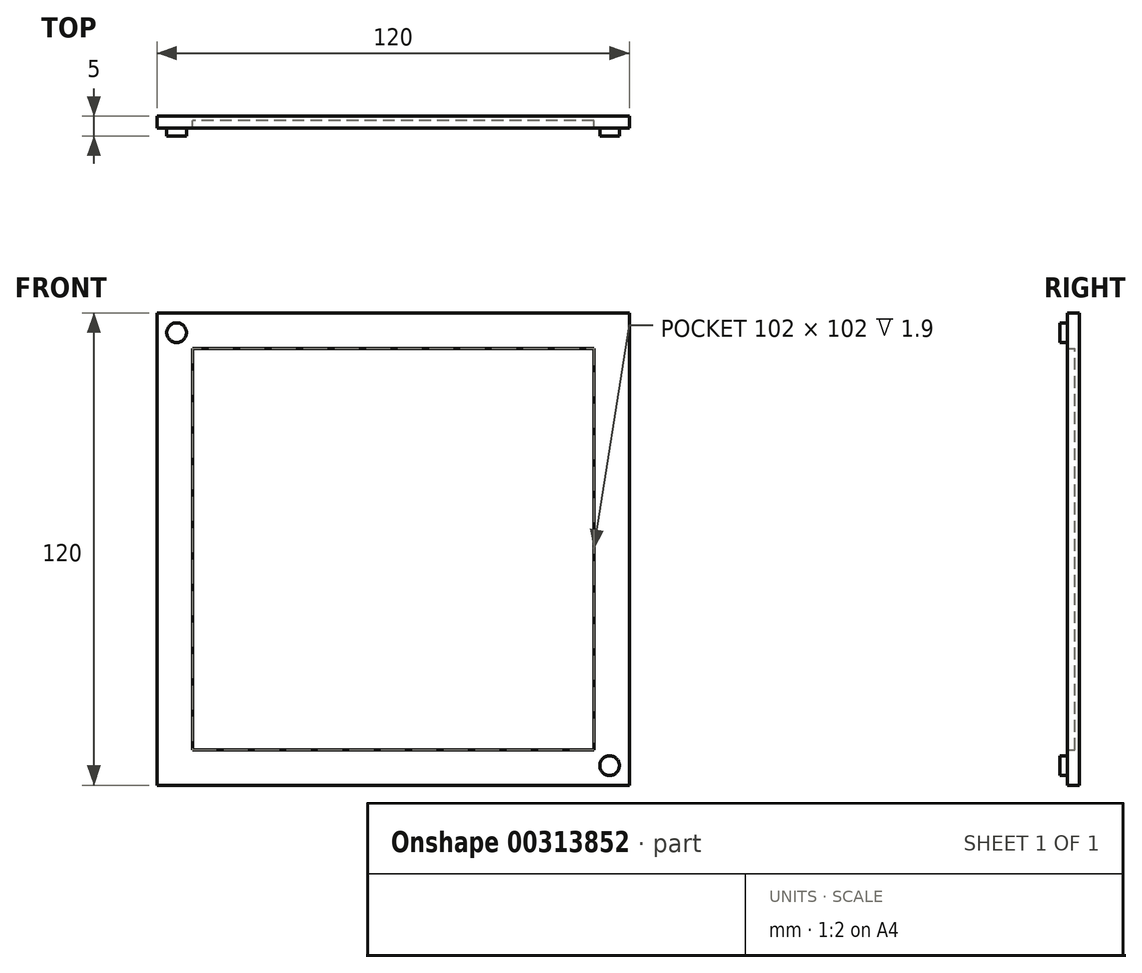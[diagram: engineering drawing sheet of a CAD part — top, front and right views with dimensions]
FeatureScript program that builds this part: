
annotation { "Feature Type Name" : "Feature", "Feature Type Description" : "" }
export const myFeature = defineFeature(function(context is Context, id is Id, definition is map)
    precondition{}
    {
        {
            var Q0;
            Q0=qCreatedBy(makeId("Front.planeOp"),FACE);
            var sketch = newSketch(context, id + "F0", { "sketchPlane" : qUnion([Q0])});
            skLineSegment(sketch, "E0.bottom", {"start": v(51, -51) * mm, "end": v(-51, -51) * mm});
            skLineSegment(sketch, "E0.top", {"start": v(51, 51) * mm, "end": v(-51, 51) * mm});
            skLineSegment(sketch, "E0.left", {"start": v(51, -51) * mm, "end": v(51, 51) * mm});
            skLineSegment(sketch, "E0.right", {"start": v(-51, -51) * mm, "end": v(-51, 51) * mm});
            skPoint(sketch, "E0.middle", {"position": v(0, 0) * mm});
            skLineSegment(sketch, "E1.bottom", {"start": v(60, -60) * mm, "end": v(-60, -60) * mm});
            skLineSegment(sketch, "E1.top", {"start": v(60, 60) * mm, "end": v(-60, 60) * mm});
            skLineSegment(sketch, "E1.left", {"start": v(60, -60) * mm, "end": v(60, 60) * mm});
            skLineSegment(sketch, "E1.right", {"start": v(-60, -60) * mm, "end": v(-60, 60) * mm});
            skSolve(sketch);
        }
        {
            var Q0;
            Q0=makeQuery(id+"F0.imprint","IMPRINT",FACE,{"disambiguationData":[TD([[makeQuery(id+"F0.imprint","IMPRINT",EDGE,{"derivedFrom":sQuery(id+"F0.wireOp",EDGE,"E0.bottom")}),1.0]])]});
            extrude(context, id + "F1", {"entities" : qUnion([Q0]), "depth" : 3 * mm});
        }
        {
            var Q0;
            Q0=makeQuery(id+"F0.imprint","IMPRINT",FACE,{"disambiguationData":[TD([[makeQuery(id+"F0.imprint","IMPRINT",EDGE,{"derivedFrom":sQuery(id+"F0.wireOp",EDGE,"E0.bottom")}),-1.0]])]});
            extrude(context, id + "F2", {"entities" : qUnion([Q0]), "operationType" : NewBodyOperationType.ADD, "depth" : 1.1 * mm});
        }
        {
            var Q0;
            Q0=makeQuery(id+"F1.opExtrude","CAP_FACE",FACE,{"disambiguationData":[OSD([sQuery(id+"F0.wireOp",EDGE,"E0.bottom"),sQuery(id+"F0.wireOp",EDGE,"E0.top"),sQuery(id+"F0.wireOp",EDGE,"E0.left"),sQuery(id+"F0.wireOp",EDGE,"E0.right"),sQuery(id+"F0.wireOp",EDGE,"E1.bottom"),sQuery(id+"F0.wireOp",EDGE,"E1.top"),sQuery(id+"F0.wireOp",EDGE,"E1.left"),sQuery(id+"F0.wireOp",EDGE,"E1.right")])],"isStart":false});
            var sketch = newSketch(context, id + "F3", { "sketchPlane" : qUnion([Q0])});
            skCircle(sketch, "E2", {"center": v(-55, 55) * mm, "radius": 2.5 * mm});
            skCircle(sketch, "E3", {"center": v(55, -55) * mm, "radius": 2.5 * mm});
            skSolve(sketch);
        }
        {
            var Q0;
            Q0=makeQuery(id+"F3.imprint","IMPRINT",FACE,{"disambiguationData":[TD([[makeQuery(id+"F3.imprint","IMPRINT",EDGE,{"derivedFrom":sQuery(id+"F3.wireOp",EDGE,"E2")}),1.0]])]});
            var Q1;
            Q1=makeQuery(id+"F3.imprint","IMPRINT",FACE,{"disambiguationData":[TD([[makeQuery(id+"F3.imprint","IMPRINT",EDGE,{"derivedFrom":sQuery(id+"F3.wireOp",EDGE,"E3")}),1.0]])]});
            extrude(context, id + "F4", {"entities" : qUnion([Q0, Q1]), "operationType" : NewBodyOperationType.ADD, "depth" : 2 * mm});
        }
    });
